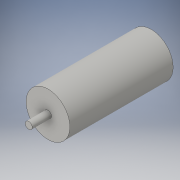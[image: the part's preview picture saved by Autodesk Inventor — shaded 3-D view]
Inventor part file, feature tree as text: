
AUTODESK INVENTOR PART (.ipt)
format: ipt  version: 2016 SP1 (Build 200210100, 210)  size: 94,208 bytes
history: native  units: in
note: dims shown in document units (in); Inventor stores cm internally (conversion verified against a paired STEP export)
features: extrude x2, sketch x2
ambient origin geometry x8: Origin, YZ Plane, XZ Plane, XY Plane, X Axis, Y Axis, Z Axis, Center Point
bodies: Solid1 (feature_tree)
feature tree (4):
  extrude  "Extrusion1"  Depth=2.3228in TaperAngle=0.0deg
  extrude  "Extrusion2"  Depth=0.4331in TaperAngle=0.0deg
  sketch  "Sketch1"  dims[d0=0.9843in d1=2.3228in d2=0.0in]
  sketch  "Sketch2"  dims[d3=0.1575in d4=0.4331in d5=0.0in]
